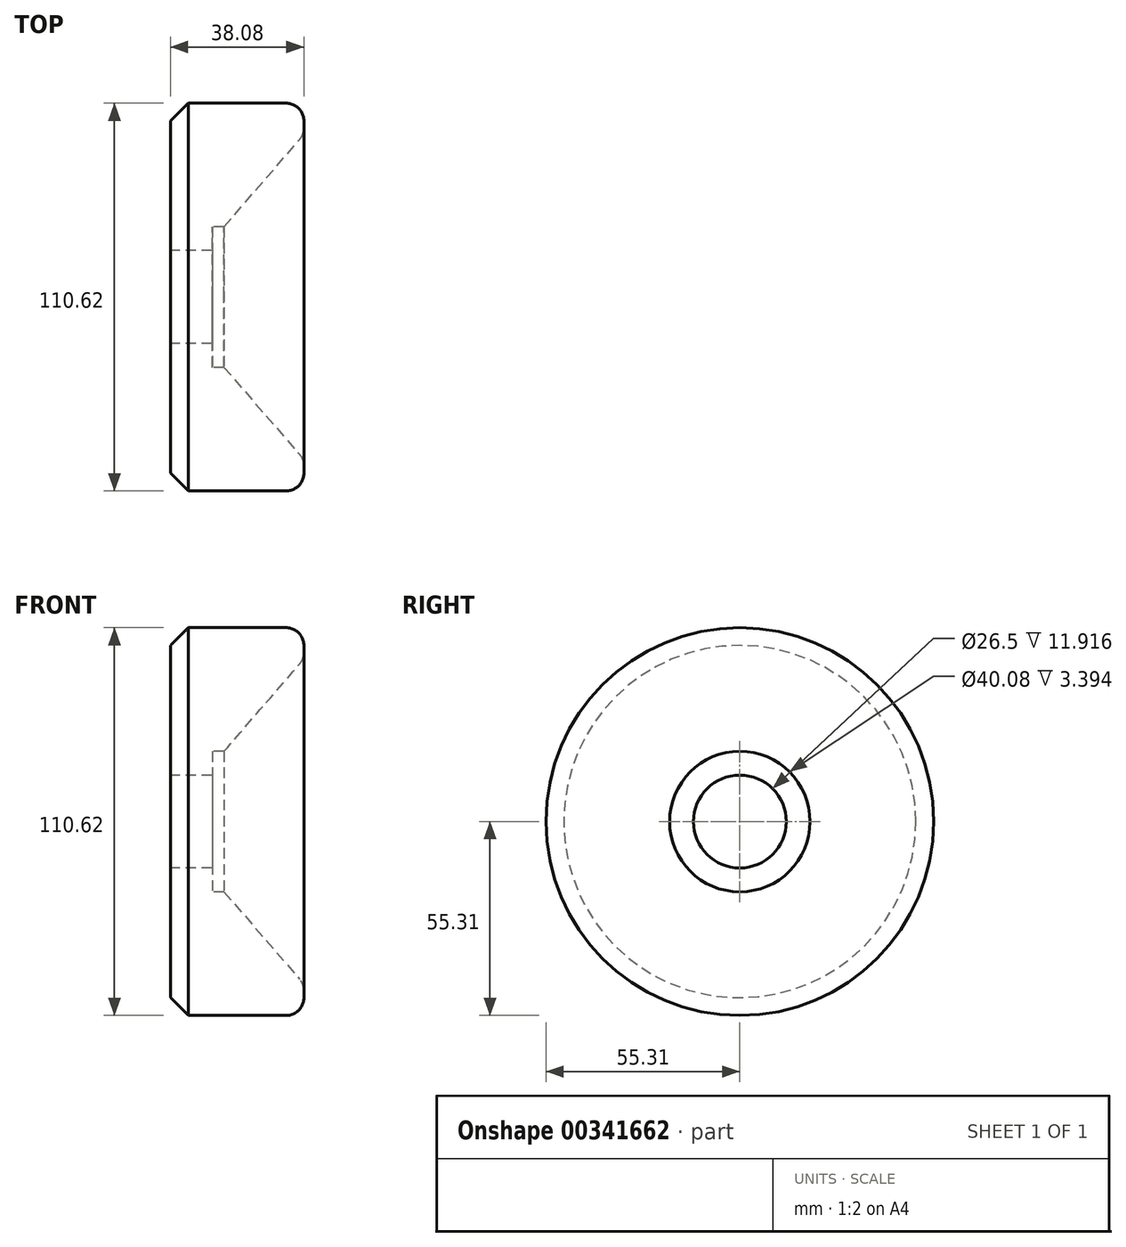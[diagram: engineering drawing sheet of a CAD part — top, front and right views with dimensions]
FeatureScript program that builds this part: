
annotation { "Feature Type Name" : "Feature", "Feature Type Description" : "" }
export const myFeature = defineFeature(function(context is Context, id is Id, definition is map)
    precondition{}
    {
        {
            var Q0;
            Q0=qCreatedBy(makeId("Front.planeOp"),FACE);
            var sketch = newSketch(context, id + "F0", { "sketchPlane" : qUnion([Q0])});
            skLineSegment(sketch, "E0", {"start": v(0, 0) * mm, "end": v(0, 55.31) * mm, "construction": true});
            skLineSegment(sketch, "E1", {"start": v(0, 0) * mm, "end": v(50.65, 0) * mm, "construction": true});
            skLineSegment(sketch, "E2", {"start": v(0, 13.25) * mm, "end": v(0, 55.31) * mm});
            skLineSegment(sketch, "E3", {"start": v(38.08, 55.31) * mm, "end": v(38.08, 46.35) * mm});
            skLineSegment(sketch, "E4", {"start": v(38.08, 46.35) * mm, "end": v(15.31, 20.04) * mm});
            skLineSegment(sketch, "E5", {"start": v(15.31, 20.04) * mm, "end": v(11.92, 20.04) * mm});
            skLineSegment(sketch, "E6", {"start": v(11.92, 20.04) * mm, "end": v(11.92, 13.25) * mm});
            skLineSegment(sketch, "E7", {"start": v(11.92, 13.25) * mm, "end": v(0, 13.25) * mm});
            skLineSegment(sketch, "E8", {"start": v(0, 55.31) * mm, "end": v(38.08, 55.31) * mm});
            skSolve(sketch);
        }
        {
            var Q0;
            Q0 = qSketchRegion(id + "F0", true);
            var Q1;
            Q1=sQuery(id+"F0.wireOp",EDGE,"E1");
            revolve(context, id + "F1", {"entities" : qUnion([Q0]), "axis" : qUnion([Q1]), "revolveType" : RevolveType.FULL});
        }
        {
            var Q0;
            Q0=makeQuery(id+"F1.opRevolve","SWEPT_EDGE",EDGE,{"disambiguationData":[OSD([sQuery(id+"F0.wireOp",EDGE,"E3"),sQuery(id+"F0.wireOp",EDGE,"E4")])]});
            var Q1;
            Q1=makeQuery(id+"F1.opRevolve","SWEPT_EDGE",EDGE,{"disambiguationData":[OSD([sQuery(id+"F0.wireOp",EDGE,"E3"),sQuery(id+"F0.wireOp",EDGE,"E8")])]});
            fillet(context, id + "F2", {"entities" : qUnion([Q0, Q1]), "radius" : 5.08 * mm, "tangentPropagation" : true, "allowEdgeOverflow" : false});
        }
        {
            var Q0;
            Q0=makeQuery(id+"F1.opRevolve","SWEPT_EDGE",EDGE,{"disambiguationData":[OSD([sQuery(id+"F0.wireOp",EDGE,"E2"),sQuery(id+"F0.wireOp",EDGE,"E8")])]});
            chamfer(context, id + "F3", {"entities" : qUnion([Q0]), "width" : 5.08 * mm, "tangentPropagation" : true});
        }
    });
